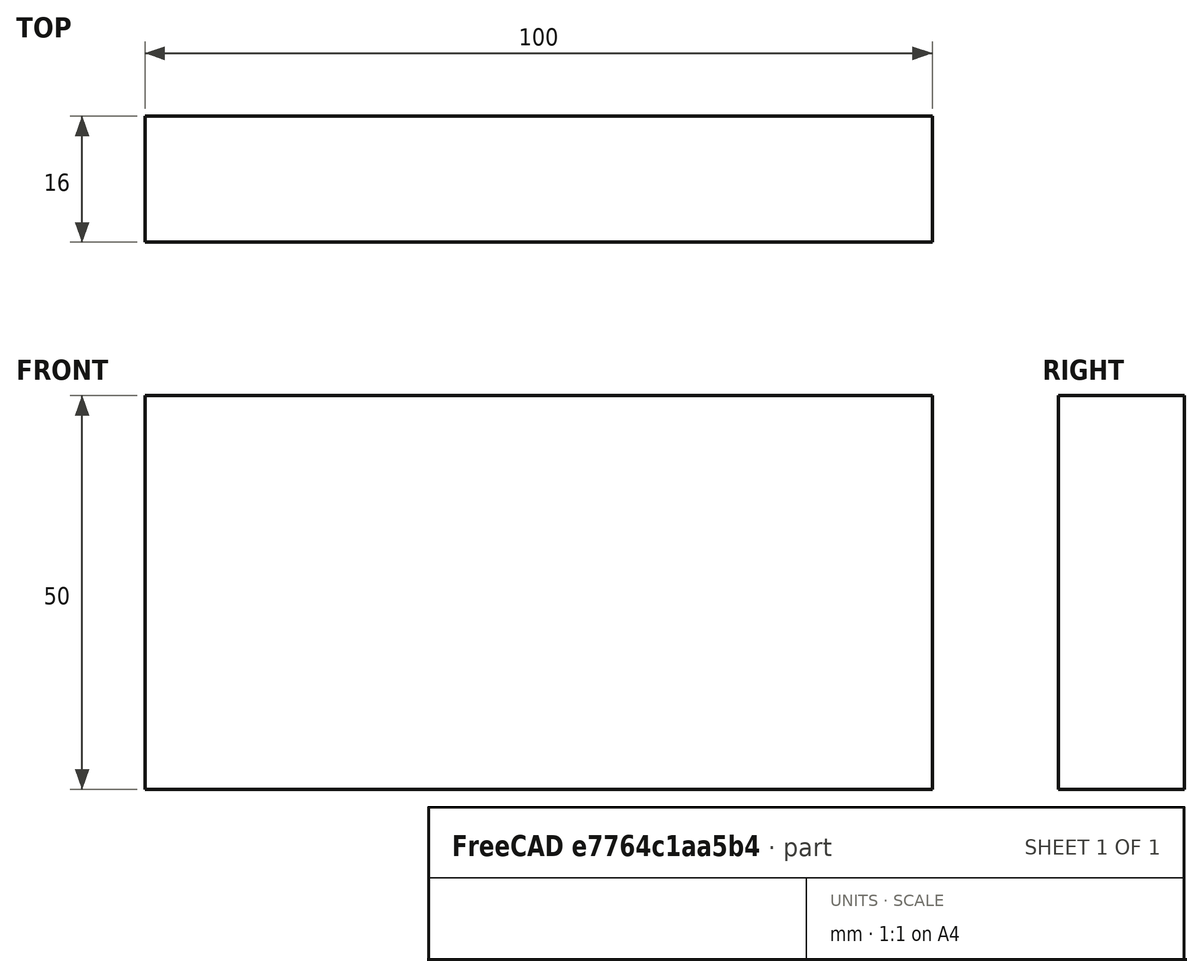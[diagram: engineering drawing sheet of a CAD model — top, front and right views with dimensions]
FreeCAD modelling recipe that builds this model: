
FCSTD DOCUMENT  (FreeCAD 0.15R4671 (Git))
Label: Flat Bar 100x16 EN10058 S235JR
License: All rights reserved
LicenseURL: http://en.wikipedia.org/wiki/All_rights_reserved
objects: Sketcher::SketchObject×1, Part::Extrusion×1
note: 2 computed .brp shape members not serialized (recipe doc carries the construction recipe); baked Part::Feature solids carry a one-line shape summary decoded from their .brp

FEATURE [Sketcher::SketchObject] Sketch
  sketch-geometry (4):
    g0: LineSegment StartX=-50 StartY=-8 StartZ=0 EndX=50 EndY=-8 EndZ=0
    g1: LineSegment StartX=50 StartY=-8 StartZ=0 EndX=50 EndY=8 EndZ=0
    g2: LineSegment StartX=50 StartY=8 StartZ=0 EndX=-50 EndY=8 EndZ=0
    g3: LineSegment StartX=-50 StartY=8 StartZ=0 EndX=-50 EndY=-8 EndZ=0
  constraints (12):
    c: Coincident(g0,g1)
    c: Coincident(g1,g2)
    c: Coincident(g2,g3)
    c: Coincident(g3,g0)
    c: Horizontal(g0)
    c: Horizontal(g2)
    c: Vertical(g1)
    c: Vertical(g3)
    c: Symmetric(g1,g2,g-2)
    c: Symmetric(g0,g1,g-1)
    c: DistanceY(g1) = 16
    c: DistanceX(g0) = 100
FEATURE [Part::Extrusion] Extrude  label="Flat Bar 100x16 EN10058 S235JR"
  Base = -> Sketch
  Dir = (0,0,50)
  Solid = true
